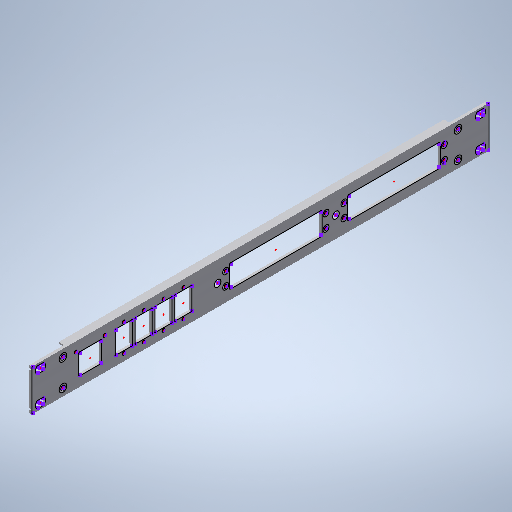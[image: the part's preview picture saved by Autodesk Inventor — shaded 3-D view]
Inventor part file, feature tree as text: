
AUTODESK INVENTOR PART (.ipt)
format: ipt  version: 2025.1 (Build 291241000, 241)  size: 1,707,520 bytes
history: native  units: in
note: dims shown in document units (in); Inventor stores cm internally (conversion verified against a paired STEP export)
features: hole x4, extrude x3, other x2
ambient origin geometry x8: Origin, YZ Plane, XZ Plane, XY Plane, X Axis, Y Axis, Z Axis, Center Point
bodies: Solid1 (feature_tree)
feature tree (9):
  other  "Schaeffer_Frontplatte"
  extrude  "Phoenix_1"  TaperAngle=0.0deg  [1 undecoded]
  hole  "Phoenix_2"  [1 undecoded]
  extrude  "Delock_1"  TaperAngle=0.0deg  [1 undecoded]
  hole  "Delock_2"  [1 undecoded]
  extrude  "Lardis_1"  [1 undecoded]
  hole  "Lardis_2"  [1 undecoded]
  hole  "Lardis_3"  [1 undecoded]
  other  "20860601_01.ipt"
note: 7 required parameter values undecoded (feature->parameter linkage not recoverable at this tier; creation-order binding heuristic only, values carry confidence <= 0.55)
